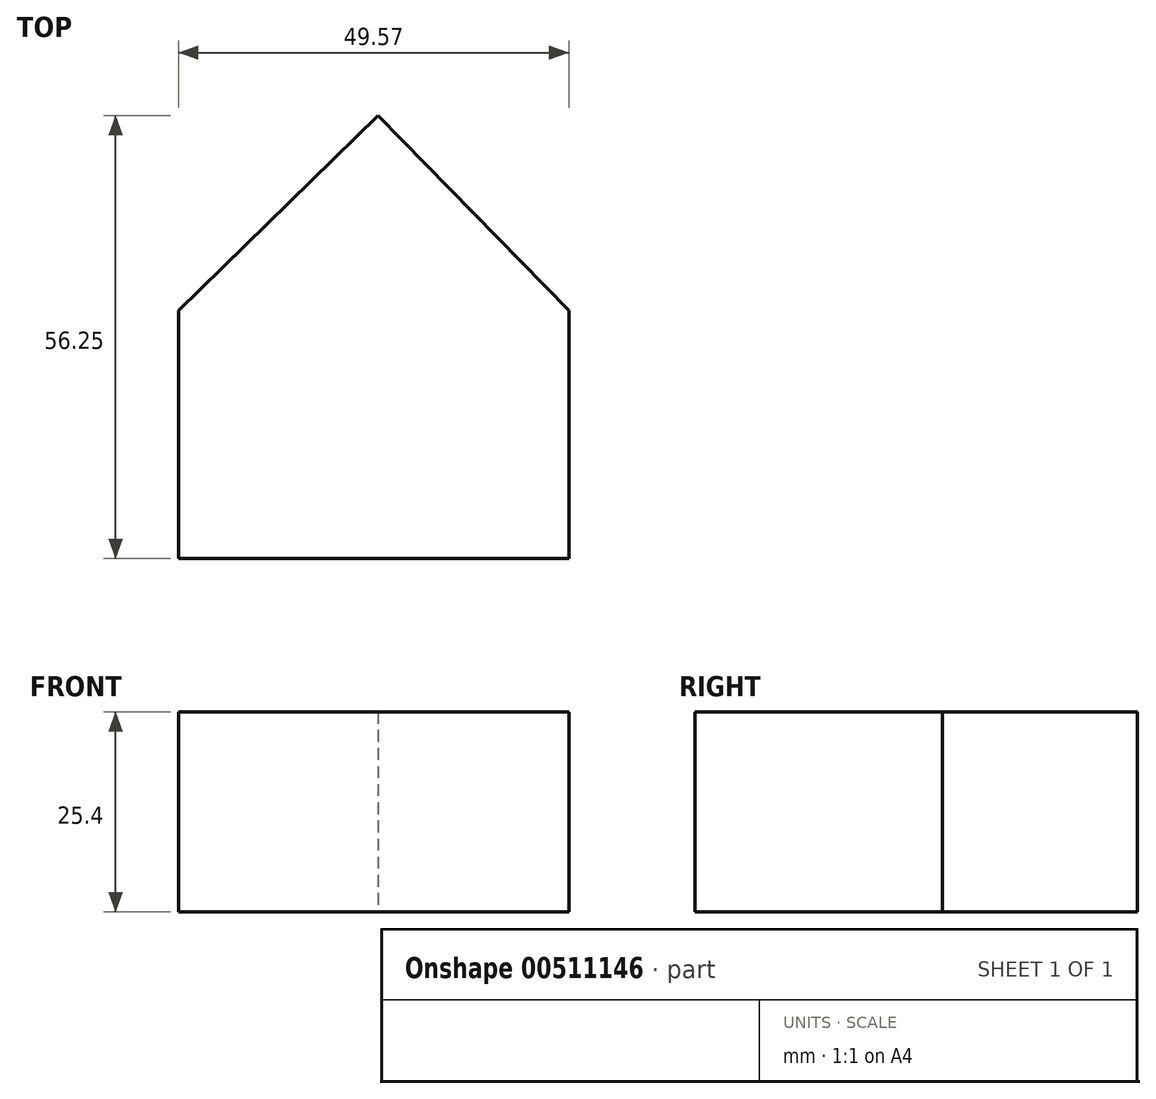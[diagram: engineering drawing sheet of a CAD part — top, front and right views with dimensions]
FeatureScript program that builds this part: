
annotation { "Feature Type Name" : "Feature", "Feature Type Description" : "" }
export const myFeature = defineFeature(function(context is Context, id is Id, definition is map)
    precondition{}
    {
        {
            var Q0;
            Q0=qCreatedBy(makeId("Top.planeOp"),FACE);
            var sketch = newSketch(context, id + "F0", { "sketchPlane" : qUnion([Q0])});
            skLineSegment(sketch, "E0", {"start": v(0, 43) * mm, "end": v(-25.36, 18.22) * mm});
            skLineSegment(sketch, "E1", {"start": v(-25.36, 18.22) * mm, "end": v(-25.36, -13.26) * mm});
            skLineSegment(sketch, "E2", {"start": v(0, 43) * mm, "end": v(24.2, 18.22) * mm});
            skLineSegment(sketch, "E3", {"start": v(24.2, 18.22) * mm, "end": v(24.2, -13.26) * mm});
            skLineSegment(sketch, "E4", {"start": v(24.2, -13.26) * mm, "end": v(-25.36, -13.26) * mm});
            skSolve(sketch);
        }
        {
            var Q0;
            Q0 = qSketchRegion(id + "F0", true);
            extrude(context, id + "F1", {"entities" : qUnion([Q0]), "endBound" : BoundingType.SYMMETRIC, "depth" : 25.4 * mm});
        }
    });
